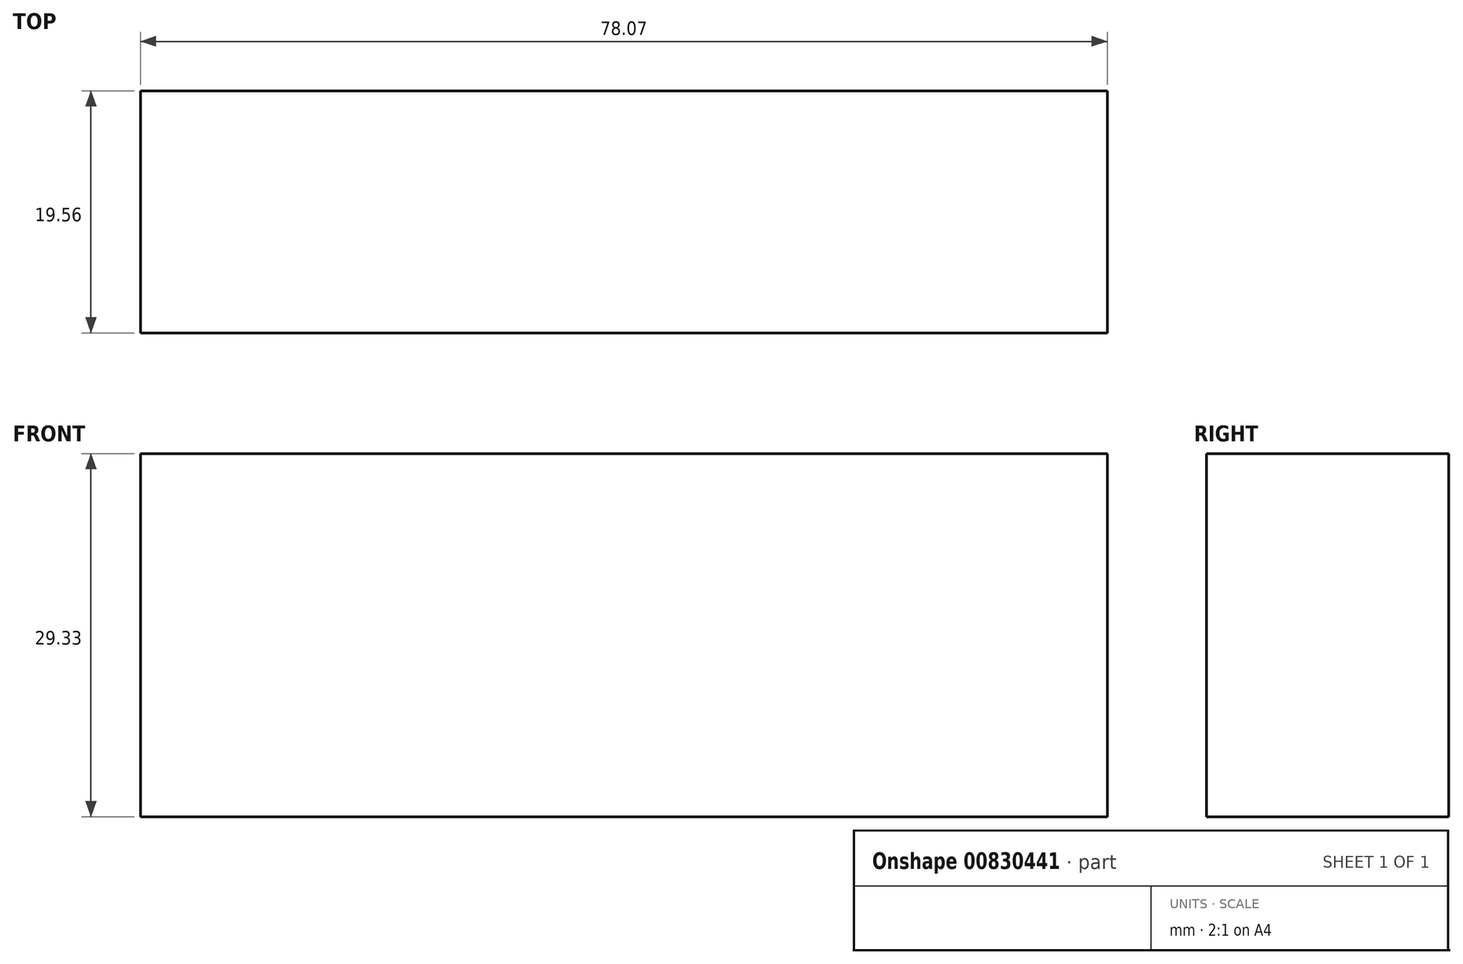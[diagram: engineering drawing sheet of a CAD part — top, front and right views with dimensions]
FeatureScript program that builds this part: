
annotation { "Feature Type Name" : "Feature", "Feature Type Description" : "" }
export const myFeature = defineFeature(function(context is Context, id is Id, definition is map)
    precondition{}
    {
        {
            var Q0;
            Q0=qCreatedBy(makeId("Front.planeOp"),FACE);
            var sketch = newSketch(context, id + "F0", { "sketchPlane" : qUnion([Q0])});
            skLineSegment(sketch, "E0.bottom", {"start": v(0, 0) * mm, "end": v(78.07, 0) * mm});
            skLineSegment(sketch, "E0.top", {"start": v(0, 29.33) * mm, "end": v(78.07, 29.33) * mm});
            skLineSegment(sketch, "E0.left", {"start": v(0, 0) * mm, "end": v(0, 29.33) * mm});
            skLineSegment(sketch, "E0.right", {"start": v(78.07, 0) * mm, "end": v(78.07, 29.33) * mm});
            skSolve(sketch);
        }
        {
            var Q0;
            Q0 = qSketchRegion(id + "F0", true);
            extrude(context, id + "F1", {"entities" : qUnion([Q0]), "depth" : 19.56 * mm, "offsetDistance" : 25.4 * mm});
        }
    });
